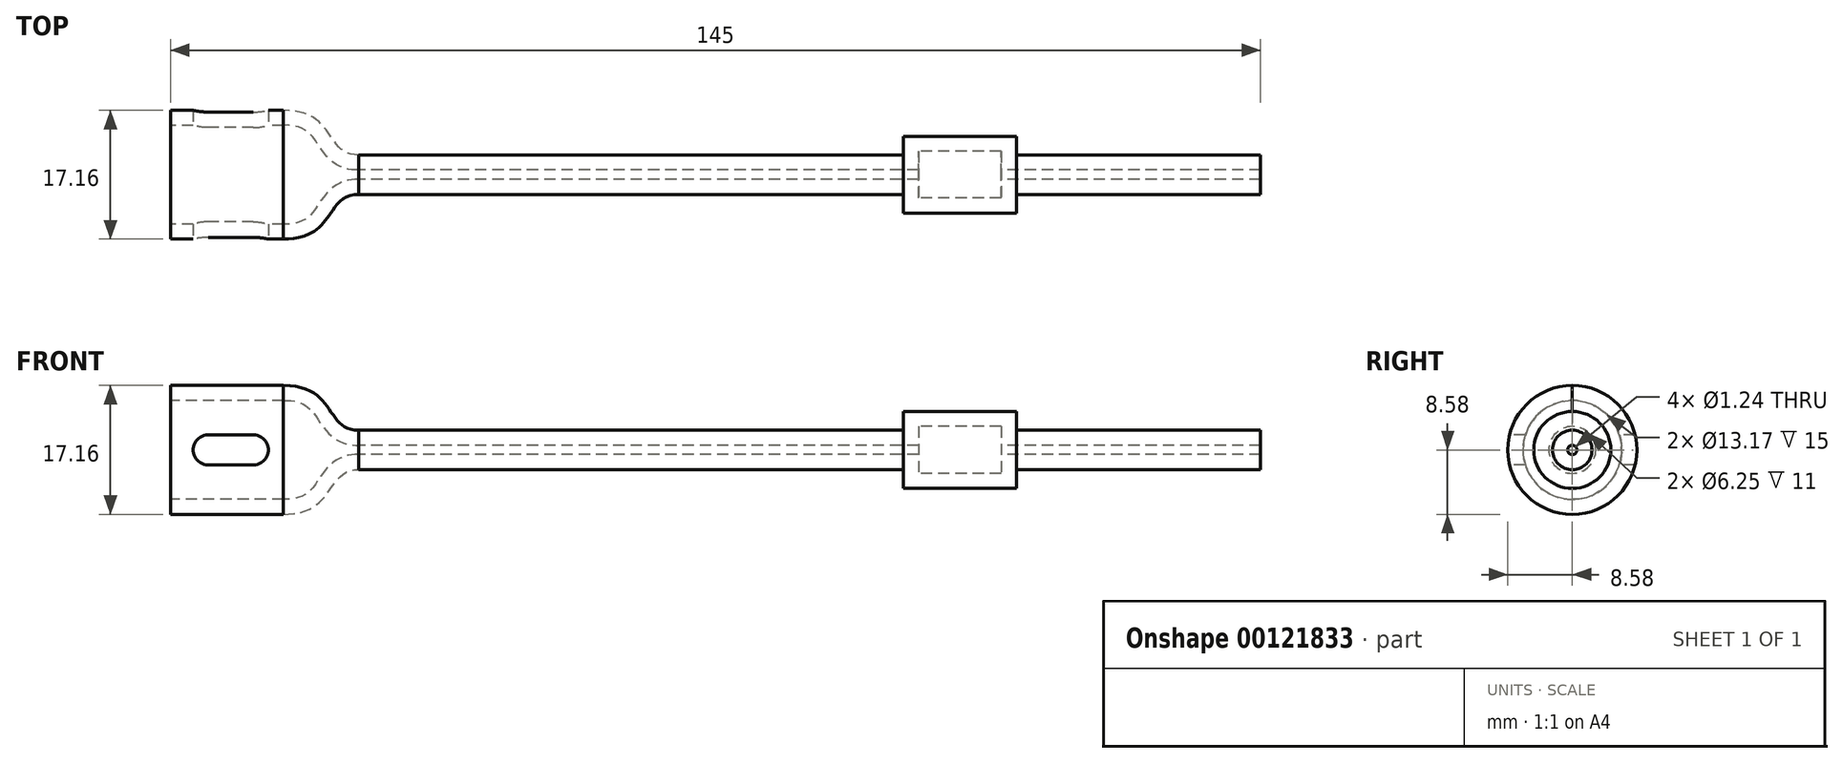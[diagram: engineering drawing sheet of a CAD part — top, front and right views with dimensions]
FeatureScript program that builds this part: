
annotation { "Feature Type Name" : "Feature", "Feature Type Description" : "" }
export const myFeature = defineFeature(function(context is Context, id is Id, definition is map)
    precondition{}
    {
        {
            var Q0;
            Q0=qCreatedBy(makeId("Front.planeOp"),FACE);
            var sketch = newSketch(context, id + "F0", { "sketchPlane" : qUnion([Q0])});
            skLineSegment(sketch, "E0.bottom", {"start": v(60, 2.62) * mm, "end": v(27.5, 2.62) * mm});
            skLineSegment(sketch, "E0.left", {"start": v(60, 2.62) * mm, "end": v(60, 0.62) * mm});
            skPoint(sketch, "E0.middle", {"position": v(0, 0) * mm});
            skLineSegment(sketch, "E1.bottom", {"start": v(27.5, 5.12) * mm, "end": v(12.5, 5.12) * mm});
            skLineSegment(sketch, "E1.left", {"start": v(27.5, 5.12) * mm, "end": v(27.5, 2.62) * mm});
            skLineSegment(sketch, "E1.right", {"start": v(12.5, 5.12) * mm, "end": v(12.5, 2.62) * mm});
            skPoint(sketch, "E1.middle", {"position": v(20, 0) * mm});
            skLineSegment(sketch, "E2.trimOffspring", {"start": v(12.5, 2.62) * mm, "end": v(-60, 2.62) * mm});
            skPoint(sketch, "E3.start.orphan", {"position": v(20, 2.62) * mm});
            skLineSegment(sketch, "E4", {"start": v(-60, 0) * mm, "end": v(60, 0) * mm});
            skFitSpline(sketch, "E5", {"points": [v(-70, 8.58) * mm, v(-60, 2.62) * mm], "startDerivative": vector(21.27, 0) * mm, "endDerivative": vector(13.56, 0.03) * mm});
            skLineSegment(sketch, "E6", {"start": v(-85, 8.58) * mm, "end": v(-70, 8.58) * mm});
            skLineSegment(sketch, "E7.0", {"start": v(60, 0.62) * mm, "end": v(25.5, 0.62) * mm});
            skLineSegment(sketch, "E7.1", {"start": v(25.5, 3.12) * mm, "end": v(25.5, 0.62) * mm});
            skLineSegment(sketch, "E7.2", {"start": v(25.5, 3.12) * mm, "end": v(14.5, 3.12) * mm});
            skLineSegment(sketch, "E7.3", {"start": v(-85, 6.58) * mm, "end": v(-70, 6.58) * mm});
            skFitSpline(sketch, "E7.4", {"points": [v(-70, 6.58) * mm, v(-69.25, 6.58) * mm, v(-68.38, 6.47) * mm, v(-67.58, 6.2) * mm, v(-67.11, 5.95) * mm, v(-66.72, 5.67) * mm, v(-66.24, 5.22) * mm, v(-65.68, 4.5) * mm, v(-65.07, 3.55) * mm, v(-64.45, 2.72) * mm, v(-63.87, 2.09) * mm, v(-63.13, 1.48) * mm, v(-62.2, 0.99) * mm, v(-61.15, 0.68) * mm, v(-60.39, 0.62) * mm, v(-60, 0.62) * mm]});
            skLineSegment(sketch, "E7.5", {"start": v(14.5, 0.62) * mm, "end": v(-60.03, 0.62) * mm});
            skLineSegment(sketch, "E7.6", {"start": v(14.5, 3.12) * mm, "end": v(14.5, 0.62) * mm});
            skLineSegment(sketch, "E8.trimOffspring", {"start": v(-85, 6.58) * mm, "end": v(-85, 8.58) * mm});
            skLineSegment(sketch, "E9", {"start": v(-60, 0) * mm, "end": v(-85, 0) * mm});
            skSolve(sketch);
        }
        {
            var Q0;
            {var subQ4=sQuery(id+"F0.wireOp",EDGE,"E0.bottom");Q0=makeQuery(id+"F0.imprint","IMPRINT",FACE,{"disambiguationData":[TD([[makeQuery(id+"F0.imprint","IMPRINT",EDGE,{"derivedFrom":subQ4}),1.0]])]});}
            var Q1;
            Q1=sQuery(id+"F0.wireOp",EDGE,"E4");
            revolve(context, id + "F1", {"entities" : qUnion([Q0]), "axis" : qUnion([Q1]), "revolveType" : RevolveType.FULL});
        }
        {
            var Q0;
            Q0=qCreatedBy(makeId("Front.planeOp"),FACE);
            var sketch = newSketch(context, id + "F2", { "sketchPlane" : qUnion([Q0])});
            skLineSegment(sketch, "E10.bottom", {"start": v(-74, 2) * mm, "end": v(-80, 2) * mm});
            skLineSegment(sketch, "E10.top", {"start": v(-74, -2) * mm, "end": v(-80, -2) * mm});
            skPoint(sketch, "E10.middle", {"position": v(-77, 0) * mm});
            skArc(sketch, "E11", {"start": v(-74, -2) * mm, "mid": v(-72, 0) * mm, "end": v(-74, 2) * mm});
            skArc(sketch, "E12", {"start": v(-80, -2) * mm, "mid": v(-82, 0) * mm, "end": v(-80, 2) * mm});
            skSolve(sketch);
        }
        {
            var Q0;
            Q0=makeQuery(id+"F2.imprint","IMPRINT",FACE,{"disambiguationData":[TD([[makeQuery(id+"F2.imprint","IMPRINT",EDGE,{"derivedFrom":sQuery(id+"F2.wireOp",EDGE,"E10.bottom")}),1.0]])]});
            extrude(context, id + "F3", {"entities" : qUnion([Q0]), "operationType" : NewBodyOperationType.REMOVE, "endBound" : BoundingType.THROUGH_ALL, "oppositeDirection" : true, "depth" : 25 * mm, "hasSecondDirection" : true, "secondDirectionBound" : SecondDirectionBoundingType.THROUGH_ALL, "secondDirectionOppositeDirection" : false, "secondDirectionDepth" : 25 * mm});
        }
    });
